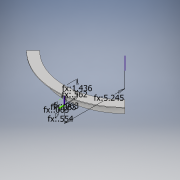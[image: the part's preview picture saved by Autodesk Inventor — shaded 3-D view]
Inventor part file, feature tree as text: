
AUTODESK INVENTOR PART (.ipt)
format: ipt  version: 2017 (Build 210142000, 142)  size: 185,856 bytes
history: native  units: in
note: dims shown in document units (in); Inventor stores cm internally (conversion verified against a paired STEP export)
features: sketch x5, extrude x4, revolve x2, plane x1
ambient origin geometry x8: Origin, YZ Plane, XZ Plane, XY Plane, X Axis, Y Axis, Z Axis, Center Point
bodies: Solid1 (feature_tree)
feature tree (12):
  revolve  "Revolution1"  [1 undecoded]
  plane  "Work Plane1"
  sketch  "Sketch2"  dims[d3=1.4364in d4=0.0625in]
  extrude  "Extrusion2"  Depth=0.0625in
  extrude  "Extrusion3"  TaperAngle=90.0deg  [1 undecoded]
  extrude  "Extrusion4"  Depth=0.375in
  extrude  "Extrusion5"  Depth=0.25in TaperAngle=0.0deg
  revolve  "Revolution2"  [1 undecoded]
  sketch  "Sketch1"  dims[d1=0.5536in d2=0.0625in]
  sketch  "Sketch3"  dims[d5=0.0625in d6=90.0deg]
  sketch  "Sketch4"  dims[d7=0.562in d8=0.375in]
  sketch  "Sketch5"  dims[d11=0.3125in d12=1.0in d13=0.0in d14=0.0156in d15=0.0in d16=0.25in d17=0.0625in d18=0.0in d19=135.0deg d20=0.0in d21=0.0in d22=0.75in d23=0.0312in d24=0.25in d25=0.25in d26=90.0deg]
note: 3 required parameter values undecoded (feature->parameter linkage not recoverable at this tier; creation-order binding heuristic only, values carry confidence <= 0.55)